# Revit family: TYCO-FPP-FireClass-FC410SNM SOUNDER OUTPUT MODULE
name_source: partatom
category: Electrical Fixtures
revit_build: Autodesk Revit 2014 (Build: 20130308_1515(x64)
units: mm (PartAtom-declared; Revit-internal decimal feet)

## types (1)
- TYCO-FPP-FireClass-FC410SNM SOUNDER OUTPUT MODULE
    Description = Sounder Circuit Controller
    EOL Resistor Value = 27k Ohm 0.5W
    Front Cover = Yes
    Keynote = Module is capable of passing up
to a maximum of 2A
    Length = 61 mm
    Manufacturer = Tyco
    Model = FireClass - 577.800.705
    Operated Current Value = 2A @ 24Vdc
    Operating Temperature = –20°C to +70°C
    PCB = PCB
    Power Requirement = 24Vdc
    RS = RS
    RS1 = RS(11)
    Rear Cover = Yes
    Relative Humidity = 10% to 95%
    ST = STT
    Storage Temperature = –40°C to +80°C
    Type Comments = The sounders are powered
from an independent power supply
    URL = https://fireclass.co.uk
    Width = 84 mm
    rs2 = RS(2)

## geometry (parser evidence)
native form markers: Sweep x6
no freeform markers — native parametric forms only
